# Revit family: QSC NL-C4
name_source: partatom
category: Communication Devices
revit_build: Autodesk Revit 2018 (Build: 20190510_1515(x64)
units: mm (PartAtom-declared; Revit-internal decimal feet)

## family parameters
Cut with Voids When Loaded = No
Host = Face
Maintain Annotation Orientation = No
Part Type = Normal
Room Calculation Point = No
Round Connector Dimension = Use Diameter
Shared = No

## types (2) — shared parameters
Communication Ports = RJ45 Q-LAN
Coverage Horizontal = 120.00°
Coverage Vertical = 120.00°
Default Elevation = 0 mm
Depth = 105 mm
Manufacturer = QSC, LLC
Manufacturer URL = http://www.qsc.com
Model = NL-C4
Product Documentation Link = https://www.qsc.com
Product Page URL = https://www.qsc.com
Regulatory Compliance = UL/IEC 62368-1, UL 2043
Temperature Max = 40° C
Temperature Min = 10° C
URL = https://www.qsc.com
Weight Product (kg) = 1.6
Weight Product (lb) = 3.5
Width = 280 mm

## per-type parameters (varying)
| type | Description | Power Handling | SPL Max |
| NL-C4 PoE | Network PoE 4-Inch Ceiling-Mount Loudspeaker | 12 | 108 |
| NL-C4 PoE+ | Network PoE+ 4-Inch Ceiling-Mount Loudspeaker | 24 | 111 |

## geometry (parser evidence)
native form markers: Blend x6, Sweep x2
no freeform markers — native parametric forms only
